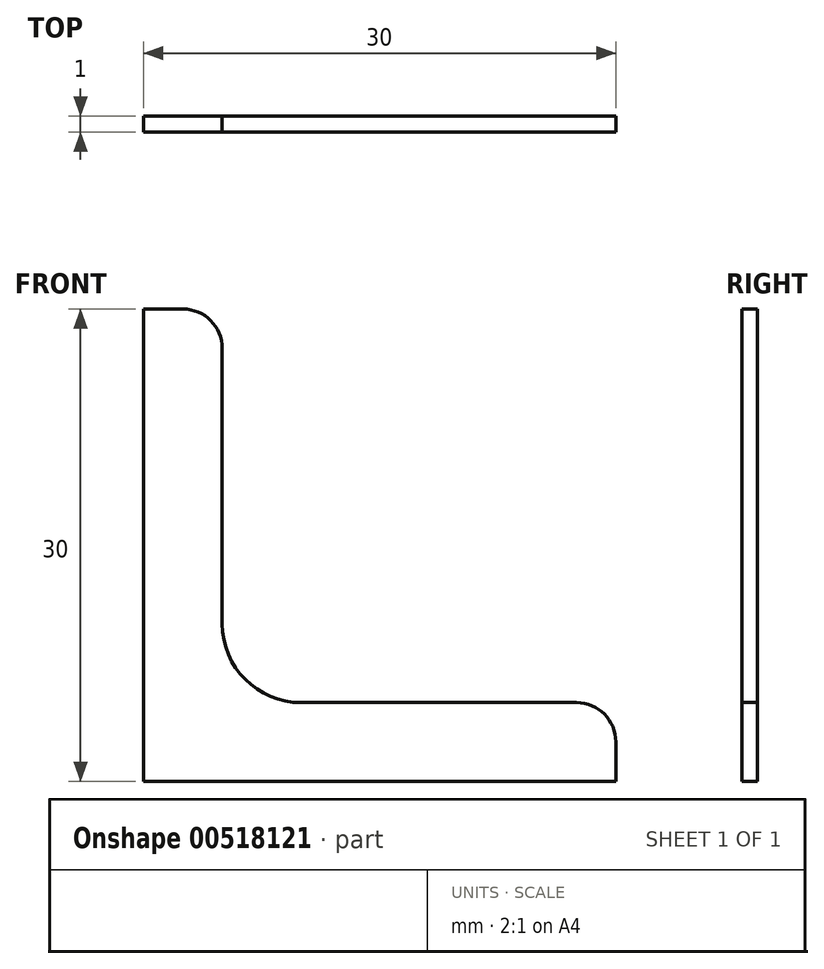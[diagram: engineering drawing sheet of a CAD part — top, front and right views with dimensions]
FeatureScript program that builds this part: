
annotation { "Feature Type Name" : "Feature", "Feature Type Description" : "" }
export const myFeature = defineFeature(function(context is Context, id is Id, definition is map)
    precondition{}
    {
        {
            var Q0;
            Q0=qCreatedBy(makeId("Front.planeOp"),FACE);
            var sketch = newSketch(context, id + "F0", { "sketchPlane" : qUnion([Q0])});
            skLineSegment(sketch, "E0.bottom", {"start": v(-15, -15) * mm, "end": v(15, -15) * mm});
            skLineSegment(sketch, "E0.top", {"start": v(-15, 15) * mm, "end": v(-12.5, 15) * mm});
            skLineSegment(sketch, "E0.left", {"start": v(-15, -15) * mm, "end": v(-15, 15) * mm});
            skLineSegment(sketch, "E0.right", {"start": v(15, -15) * mm, "end": v(15, -12.5) * mm});
            skPoint(sketch, "E0.middle", {"position": v(0, 0) * mm});
            skLineSegment(sketch, "E1.top", {"start": v(12.5, -10) * mm, "end": v(-5, -10) * mm});
            skLineSegment(sketch, "E1.right", {"start": v(-10, 12.5) * mm, "end": v(-10, -5) * mm});
            skArc(sketch, "E2.filletArc", {"start": v(15, -12.5) * mm, "mid": v(14.27, -10.73) * mm, "end": v(12.5, -10) * mm});
            skArc(sketch, "E3.filletArc", {"start": v(-10, 12.5) * mm, "mid": v(-10.73, 14.27) * mm, "end": v(-12.5, 15) * mm});
            skPoint(sketch, "E4.visualSharp", {"position": v(-10, -10) * mm});
            skArc(sketch, "E4.filletArc", {"start": v(-10, -5) * mm, "mid": v(-8.54, -8.54) * mm, "end": v(-5, -10) * mm});
            skSolve(sketch);
        }
        {
            var Q0;
            {var subQ1=sQuery(id+"F0.wireOp",EDGE,"E0.top");Q0=makeQuery(id+"F0.imprint","IMPRINT",FACE,{"disambiguationData":[TD([[makeQuery(id+"F0.imprint","IMPRINT",EDGE,{"derivedFrom":subQ1}),-1.0]])]});}
            extrude(context, id + "F1", {"entities" : qUnion([Q0]), "offsetDistance" : 25 * mm, "depth" : 1 * mm});
        }
    });
